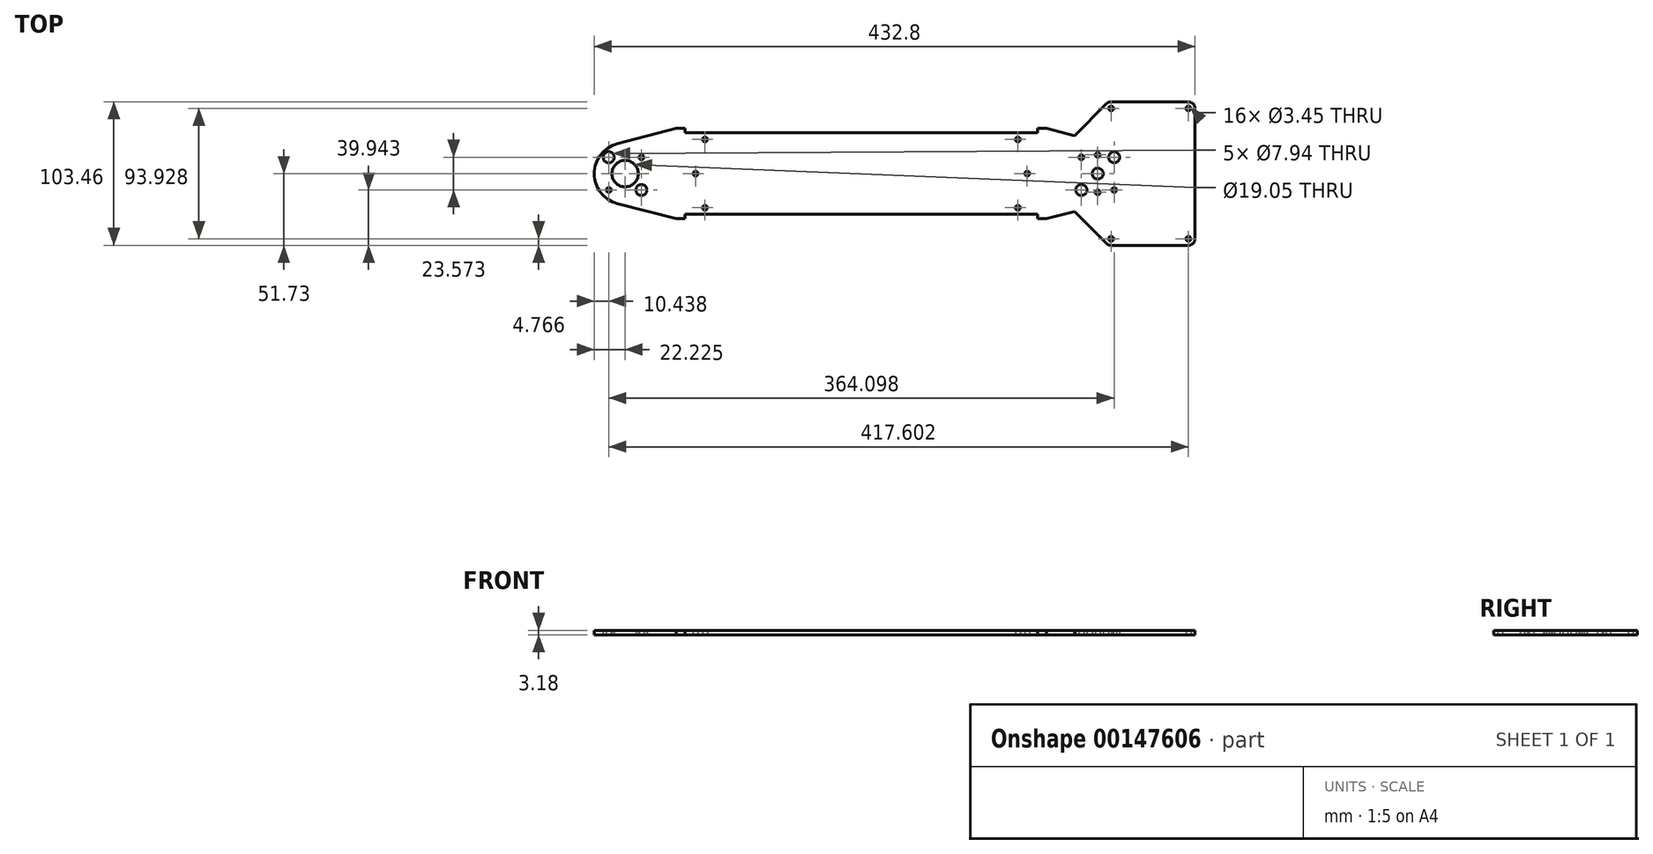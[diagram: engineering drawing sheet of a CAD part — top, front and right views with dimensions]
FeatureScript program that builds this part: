
annotation { "Feature Type Name" : "Feature", "Feature Type Description" : "" }
export const myFeature = defineFeature(function(context is Context, id is Id, definition is map)
    precondition{}
    {
        {
            var Q0;
            Q0=qCreatedBy(makeId("Top.planeOp"),FACE);
            var sketch = newSketch(context, id + "F0", { "sketchPlane" : qUnion([Q0])});
            skPoint(sketch, "E0.rect.middle", {"position": v(0, 0) * mm});
            skCircle(sketch, "E1", {"center": v(0, 0) * mm, "radius": 3.97 * mm});
            skLineSegment(sketch, "E2.bottom", {"start": v(11.79, 11.79) * mm, "end": v(-11.79, 11.79) * mm, "construction": true});
            skLineSegment(sketch, "E2.left", {"start": v(11.79, 11.79) * mm, "end": v(11.79, -11.79) * mm, "construction": true});
            skLineSegment(sketch, "E2.right", {"start": v(-11.79, 11.79) * mm, "end": v(-11.79, -11.79) * mm, "construction": true});
            skCircle(sketch, "E3", {"center": v(-11.79, 11.79) * mm, "radius": 1.73 * mm});
            skCircle(sketch, "E4", {"center": v(11.79, 11.79) * mm, "radius": 3.97 * mm});
            skCircle(sketch, "E5", {"center": v(11.79, -11.79) * mm, "radius": 1.73 * mm});
            skCircle(sketch, "E6", {"center": v(-11.79, -11.79) * mm, "radius": 3.97 * mm});
            skArc(sketch, "E7", {"start": v(-346.1, 21.51) * mm, "mid": v(-362.75, 0) * mm, "end": v(-346.1, -21.51) * mm});
            skLineSegment(sketch, "E8.bottom", {"start": v(-352.31, 11.79) * mm, "end": v(-328.74, 11.79) * mm, "construction": true});
            skLineSegment(sketch, "E8.top", {"start": v(-352.31, -11.79) * mm, "end": v(-328.74, -11.79) * mm, "construction": true});
            skLineSegment(sketch, "E8.left", {"start": v(-352.31, 11.79) * mm, "end": v(-352.31, -11.79) * mm, "construction": true});
            skLineSegment(sketch, "E8.right", {"start": v(-328.74, 11.79) * mm, "end": v(-328.74, -11.79) * mm, "construction": true});
            skCircle(sketch, "E9", {"center": v(-328.74, 11.79) * mm, "radius": 1.73 * mm});
            skCircle(sketch, "E10", {"center": v(-340.53, 0) * mm, "radius": 9.53 * mm});
            skCircle(sketch, "E11", {"center": v(-352.31, 11.79) * mm, "radius": 3.97 * mm});
            skCircle(sketch, "E12", {"center": v(-352.31, -11.79) * mm, "radius": 1.73 * mm});
            skCircle(sketch, "E13", {"center": v(-328.74, -11.79) * mm, "radius": 3.97 * mm});
            skLineSegment(sketch, "E14", {"start": v(0, 0) * mm, "end": v(-340.53, 0) * mm, "construction": true});
            skLineSegment(sketch, "E15", {"start": v(-346.1, -21.51) * mm, "end": v(-303.61, -32.54) * mm});
            skLineSegment(sketch, "E16", {"start": v(-346.1, 21.51) * mm, "end": v(-303.61, 32.54) * mm});
            skLineSegment(sketch, "E17", {"start": v(-297.26, -29.37) * mm, "end": v(-43.26, -29.37) * mm});
            skLineSegment(sketch, "E18", {"start": v(-297.26, 29.37) * mm, "end": v(-43.26, 29.37) * mm});
            skLineSegment(sketch, "E19", {"start": v(-297.26, 32.54) * mm, "end": v(-297.26, 29.37) * mm});
            skLineSegment(sketch, "E20", {"start": v(-297.26, 32.54) * mm, "end": v(-303.61, 32.54) * mm});
            skLineSegment(sketch, "E21", {"start": v(-297.26, -29.37) * mm, "end": v(-297.26, -32.54) * mm});
            skLineSegment(sketch, "E22", {"start": v(-297.26, -32.54) * mm, "end": v(-303.61, -32.54) * mm});
            skLineSegment(sketch, "E23", {"start": v(-43.26, -29.37) * mm, "end": v(-43.26, -32.54) * mm});
            skLineSegment(sketch, "E24", {"start": v(-43.26, -32.54) * mm, "end": v(-36.91, -32.54) * mm});
            skLineSegment(sketch, "E25", {"start": v(-43.26, 29.37) * mm, "end": v(-43.26, 32.54) * mm});
            skLineSegment(sketch, "E26", {"start": v(-43.26, 32.54) * mm, "end": v(-36.91, 32.54) * mm});
            skLineSegment(sketch, "E27", {"start": v(-36.91, -32.54) * mm, "end": v(-16.77, -27.32) * mm});
            skLineSegment(sketch, "E28", {"start": v(-16.77, 27.32) * mm, "end": v(-36.91, 32.54) * mm});
            skLineSegment(sketch, "E29", {"start": v(-297.26, 29.37) * mm, "end": v(-297.26, 24.6) * mm, "construction": true});
            skLineSegment(sketch, "E30", {"start": v(-297.26, 24.6) * mm, "end": v(-282.98, 24.6) * mm, "construction": true});
            skLineSegment(sketch, "E31", {"start": v(-297.26, -29.37) * mm, "end": v(-297.26, -24.6) * mm, "construction": true});
            skLineSegment(sketch, "E32", {"start": v(-297.26, -24.6) * mm, "end": v(-282.98, -24.6) * mm, "construction": true});
            skLineSegment(sketch, "E33", {"start": v(-43.26, -29.37) * mm, "end": v(-43.26, -24.6) * mm, "construction": true});
            skLineSegment(sketch, "E34", {"start": v(-43.26, -24.6) * mm, "end": v(-57.55, -24.6) * mm, "construction": true});
            skLineSegment(sketch, "E35", {"start": v(-43.26, 29.37) * mm, "end": v(-43.26, 24.6) * mm, "construction": true});
            skLineSegment(sketch, "E36", {"start": v(-43.26, 24.6) * mm, "end": v(-57.55, 24.6) * mm, "construction": true});
            skCircle(sketch, "E37", {"center": v(-282.98, 24.6) * mm, "radius": 1.73 * mm});
            skCircle(sketch, "E38", {"center": v(-57.55, 24.6) * mm, "radius": 1.73 * mm});
            skCircle(sketch, "E39", {"center": v(-57.55, -24.6) * mm, "radius": 1.73 * mm});
            skCircle(sketch, "E40", {"center": v(-282.98, -24.6) * mm, "radius": 1.73 * mm});
            skLineSegment(sketch, "E41", {"start": v(-11.79, -11.79) * mm, "end": v(11.79, -11.79) * mm, "construction": true});
            skLineSegment(sketch, "E42", {"start": v(-170.26, -29.37) * mm, "end": v(-170.26, 0) * mm, "construction": true});
            skLineSegment(sketch, "E43", {"start": v(-170.26, 0) * mm, "end": v(-170.26, 29.37) * mm, "construction": true});
            skLineSegment(sketch, "E44", {"start": v(-328.74, 11.79) * mm, "end": v(-289.73, 11.79) * mm, "construction": true});
            skLineSegment(sketch, "E45", {"start": v(-289.73, 11.79) * mm, "end": v(-289.73, 0) * mm, "construction": true});
            skLineSegment(sketch, "E46", {"start": v(-11.79, 11.79) * mm, "end": v(-50.8, 11.79) * mm, "construction": true});
            skLineSegment(sketch, "E47", {"start": v(-50.8, 11.79) * mm, "end": v(-50.8, 0) * mm, "construction": true});
            skCircle(sketch, "E48", {"center": v(-289.73, 0) * mm, "radius": 1.73 * mm});
            skCircle(sketch, "E49", {"center": v(-50.8, 0) * mm, "radius": 1.73 * mm});
            skLineSegment(sketch, "E50", {"start": v(-16.77, 27.32) * mm, "end": v(5.58, 21.51) * mm, "construction": true});
            skLineSegment(sketch, "E51", {"start": v(-16.77, -27.32) * mm, "end": v(5.58, -21.51) * mm, "construction": true});
            skLineSegment(sketch, "E52", {"start": v(0, 0) * mm, "end": v(70.05, 0) * mm, "construction": true});
            skLineSegment(sketch, "E53", {"start": v(70.05, 0) * mm, "end": v(70.05, 0) * mm});
            skLineSegment(sketch, "E54", {"start": v(-16.77, 27.32) * mm, "end": v(6.25, 50.33) * mm});
            skLineSegment(sketch, "E55", {"start": v(-16.77, -27.32) * mm, "end": v(6.25, -50.33) * mm});
            skArc(sketch, "E56", {"start": v(5.58, -21.51) * mm, "mid": v(22.23, 0) * mm, "end": v(5.58, 21.51) * mm, "construction": true});
            skCircle(sketch, "E57", {"center": v(9.61, 46.96) * mm, "radius": 1.73 * mm});
            skArc(sketch, "E58", {"start": v(9.61, 51.73) * mm, "mid": v(7.8, 51.36) * mm, "end": v(6.25, 50.33) * mm});
            skLineSegment(sketch, "E59", {"start": v(9.61, 51.73) * mm, "end": v(70.05, 51.73) * mm});
            skLineSegment(sketch, "E60", {"start": v(70.05, 51.73) * mm, "end": v(70.05, -51.73) * mm});
            skLineSegment(sketch, "E61", {"start": v(70.05, -51.73) * mm, "end": v(9.61, -51.73) * mm});
            skArc(sketch, "E62", {"start": v(6.25, -50.33) * mm, "mid": v(7.8, -51.36) * mm, "end": v(9.61, -51.73) * mm});
            skLineSegment(sketch, "E63", {"start": v(0, -13.5) * mm, "end": v(0, 13.5) * mm, "construction": true});
            skCircle(sketch, "E64", {"center": v(0, 13.5) * mm, "radius": 1.73 * mm});
            skCircle(sketch, "E65", {"center": v(0, -13.5) * mm, "radius": 1.73 * mm});
            skCircle(sketch, "E66", {"center": v(0, 0) * mm, "radius": 7.14 * mm, "construction": true});
            skCircle(sketch, "E67", {"center": v(0, 13.5) * mm, "radius": 6.35 * mm, "construction": true});
            skLineSegment(sketch, "E68.bottom", {"start": v(9.61, 46.96) * mm, "end": v(65.29, 46.96) * mm, "construction": true});
            skLineSegment(sketch, "E68.top", {"start": v(9.61, -46.96) * mm, "end": v(65.29, -46.96) * mm, "construction": true});
            skLineSegment(sketch, "E68.left", {"start": v(9.61, 46.96) * mm, "end": v(9.61, -46.96) * mm, "construction": true});
            skLineSegment(sketch, "E68.right", {"start": v(65.29, 46.96) * mm, "end": v(65.29, -46.96) * mm, "construction": true});
            skPoint(sketch, "E68.middle", {"position": v(37.45, 0) * mm});
            skLineSegment(sketch, "E69", {"start": v(65.29, 46.96) * mm, "end": v(65.29, 51.73) * mm, "construction": true});
            skLineSegment(sketch, "E70", {"start": v(65.29, 46.96) * mm, "end": v(70.05, 46.96) * mm, "construction": true});
            skLineSegment(sketch, "E71", {"start": v(9.61, 46.96) * mm, "end": v(9.61, 51.73) * mm, "construction": true});
            skCircle(sketch, "E72", {"center": v(65.29, 46.96) * mm, "radius": 1.73 * mm});
            skCircle(sketch, "E73", {"center": v(65.29, -46.96) * mm, "radius": 1.73 * mm});
            skCircle(sketch, "E74", {"center": v(9.61, -46.96) * mm, "radius": 1.73 * mm});
            skSolve(sketch);
        }
        {
            var Q0;
            Q0=qSketchRegion(id+"F0",true);
            extrude(context, id + "F1", {"entities" : qUnion([Q0]), "depth" : 3.17 * mm});
        }
        {
            var Q0;
            Q0=makeQuery(id+"F1.opExtrude","SWEPT_EDGE",EDGE,{"disambiguationData":[OSD([sQuery(id+"F0.wireOp",EDGE,"E59"),sQuery(id+"F0.wireOp",EDGE,"E60")])]});
            var Q1;
            Q1=makeQuery(id+"F1.opExtrude","SWEPT_EDGE",EDGE,{"disambiguationData":[OSD([sQuery(id+"F0.wireOp",EDGE,"E60"),sQuery(id+"F0.wireOp",EDGE,"E61")])]});
            fillet(context, id + "F2", {"entities" : qUnion([Q0, Q1]), "radius" : 4.76 * mm, "tangentPropagation" : true, "allowEdgeOverflow" : false});
        }
    });
